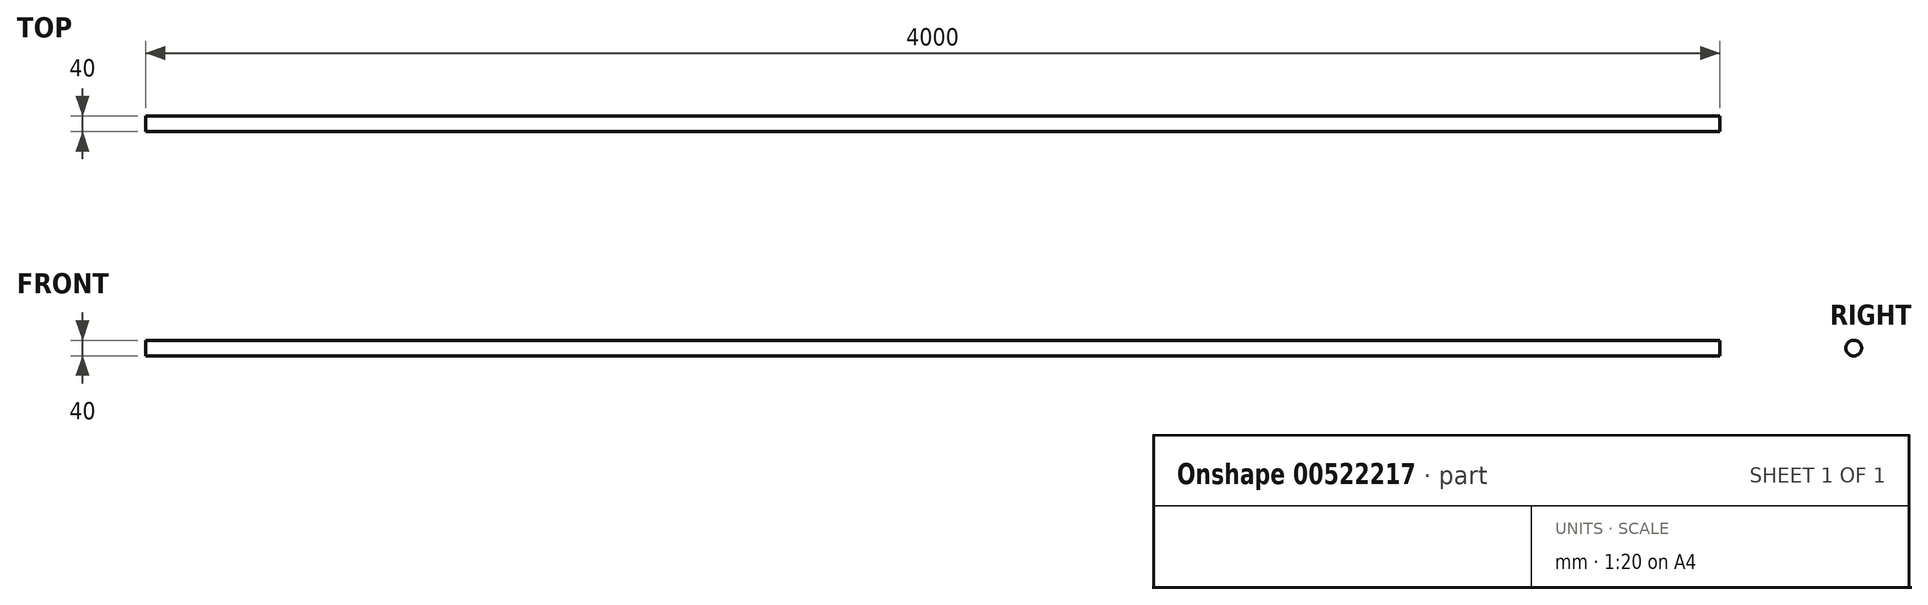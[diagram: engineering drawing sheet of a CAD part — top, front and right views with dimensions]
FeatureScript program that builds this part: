
annotation { "Feature Type Name" : "Feature", "Feature Type Description" : "" }
export const myFeature = defineFeature(function(context is Context, id is Id, definition is map)
    precondition{}
    {
        {
            var Q0;
            Q0=qCreatedBy(makeId("Right.planeOp"),FACE);
            var sketch = newSketch(context, id + "F0", { "sketchPlane" : qUnion([Q0])});
            skCircle(sketch, "E0", {"center": v(0, 0) * mm, "radius": 20 * mm});
            skSolve(sketch);
        }
        {
            var Q0;
            Q0 = qSketchRegion(id + "F0", true);
            extrude(context, id + "F1", {"entities" : qUnion([Q0]), "depth" : 4000 * mm, "offsetDistance" : 25 * mm});
        }
    });
